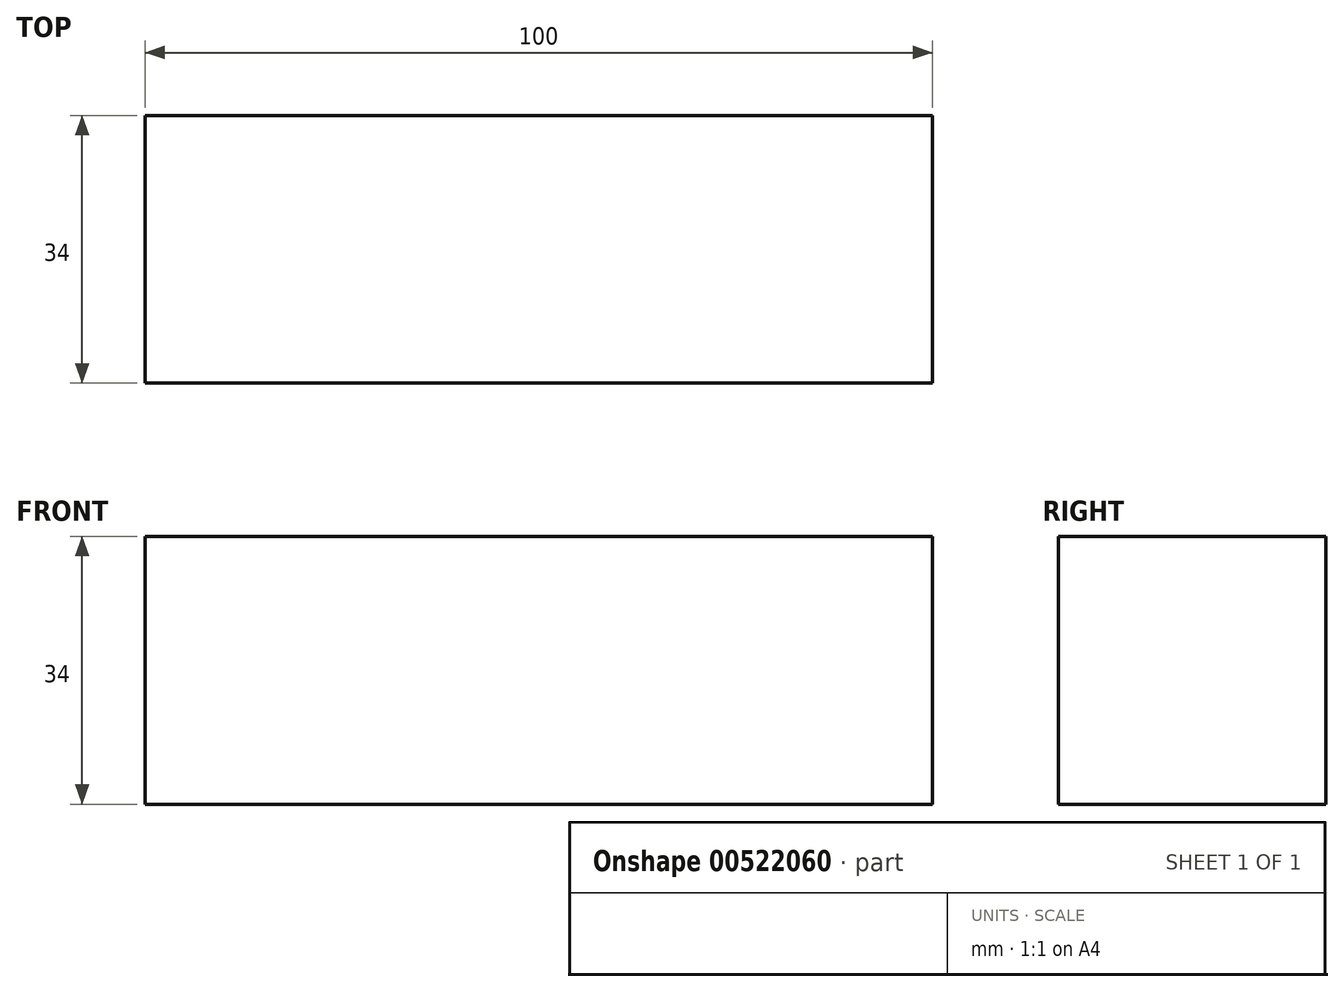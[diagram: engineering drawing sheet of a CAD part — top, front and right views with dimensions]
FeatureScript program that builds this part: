
annotation { "Feature Type Name" : "Feature", "Feature Type Description" : "" }
export const myFeature = defineFeature(function(context is Context, id is Id, definition is map)
    precondition{}
    {
        {
            var Q0;
            Q0=qCreatedBy(makeId("Right.planeOp"),FACE);
            var sketch = newSketch(context, id + "F0", { "sketchPlane" : qUnion([Q0])});
            skLineSegment(sketch, "E0.bottom", {"start": v(0, 0) * mm, "end": v(-34, 0) * mm});
            skLineSegment(sketch, "E0.top", {"start": v(0, 34) * mm, "end": v(-34, 34) * mm});
            skLineSegment(sketch, "E0.left", {"start": v(0, 0) * mm, "end": v(0, 34) * mm});
            skLineSegment(sketch, "E0.right", {"start": v(-34, 0) * mm, "end": v(-34, 34) * mm});
            skSolve(sketch);
        }
        {
            var Q0;
            Q0=makeQuery(id+"F0.imprint","IMPRINT",FACE,{"disambiguationData":[TD([[makeQuery(id+"F0.imprint","IMPRINT",EDGE,{"derivedFrom":sQuery(id+"F0.wireOp",EDGE,"E0.bottom")}),-1.0]])]});
            extrude(context, id + "F1", {"entities" : qUnion([Q0]), "oppositeDirection" : true, "depth" : 100 * mm, "offsetDistance" : 25 * mm});
        }
    });
